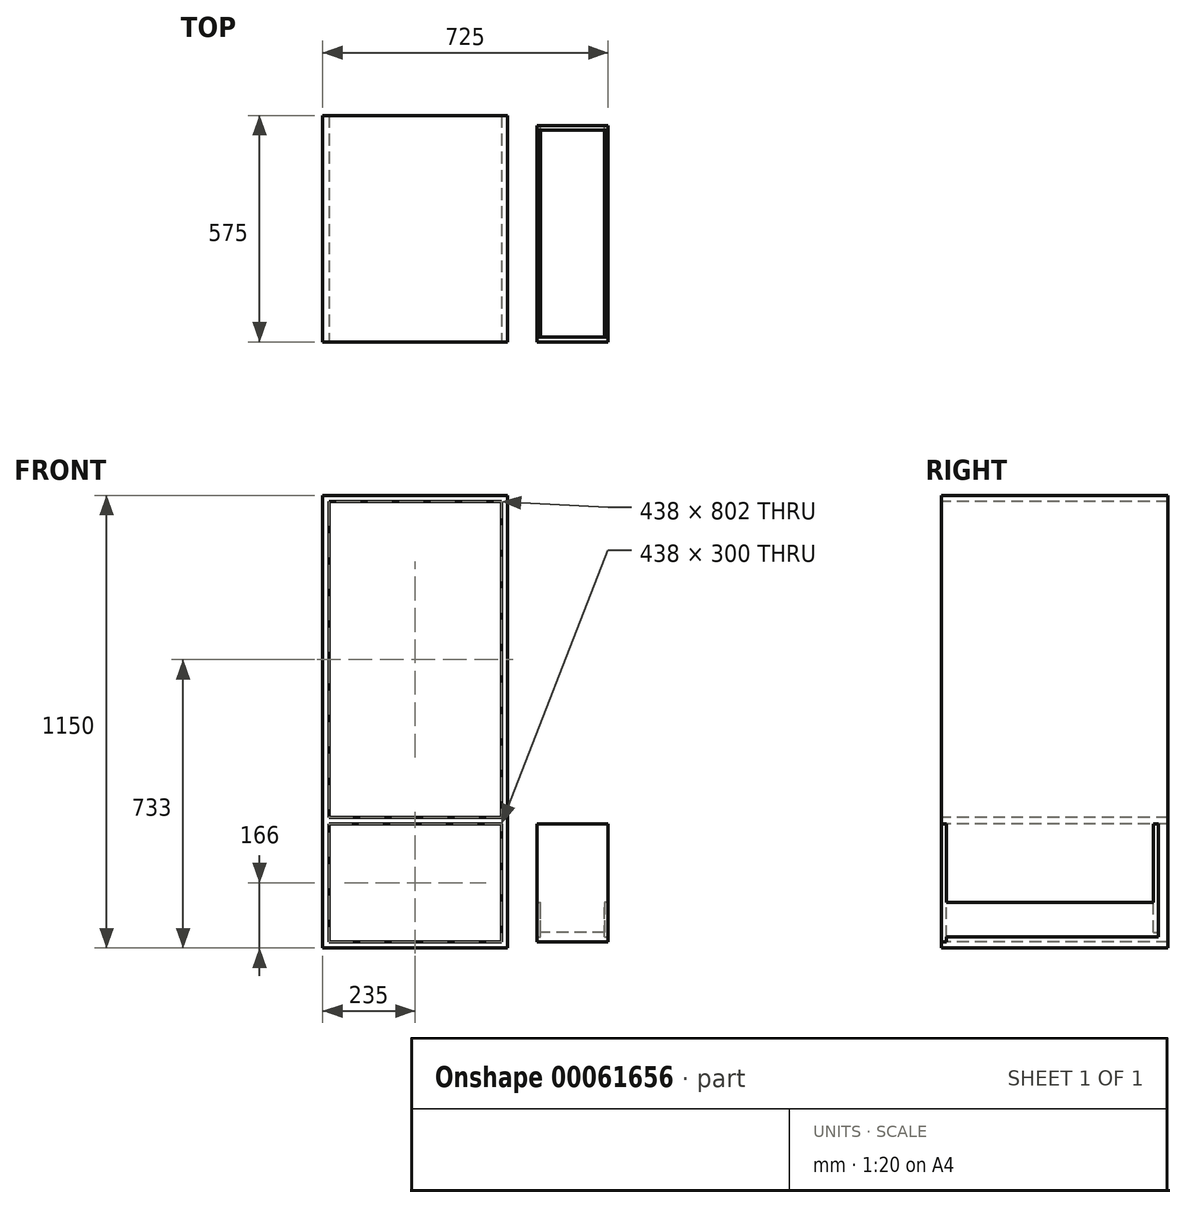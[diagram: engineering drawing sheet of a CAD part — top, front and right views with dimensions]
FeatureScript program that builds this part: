
annotation { "Feature Type Name" : "Feature", "Feature Type Description" : "" }
export const myFeature = defineFeature(function(context is Context, id is Id, definition is map)
    precondition{}
    {
        {
            var Q0;
            Q0=qCreatedBy(makeId("Front.planeOp"),FACE);
            var sketch = newSketch(context, id + "F0", { "sketchPlane" : qUnion([Q0])});
            skLineSegment(sketch, "E0.bottom", {"start": v(0, 0) * mm, "end": v(470, 0) * mm});
            skLineSegment(sketch, "E0.top", {"start": v(0, 1150) * mm, "end": v(470, 1150) * mm});
            skLineSegment(sketch, "E0.left", {"start": v(0, 0) * mm, "end": v(0, 1150) * mm});
            skLineSegment(sketch, "E0.right", {"start": v(470, 0) * mm, "end": v(470, 1150) * mm});
            skSolve(sketch);
        }
        {
            var Q0;
            Q0=makeQuery(id+"F0.imprint","IMPRINT",FACE,{"disambiguationData":[TD([[makeQuery(id+"F0.imprint","IMPRINT",EDGE,{"derivedFrom":sQuery(id+"F0.wireOp",EDGE,"E0.bottom")}),1.0]])]});
            extrude(context, id + "F1", {"entities" : qUnion([Q0]), "oppositeDirection" : true, "depth" : 575 * mm});
        }
        {
            var Q0;
            Q0=makeQuery(id+"F1.opExtrude","CAP_FACE",FACE,{"disambiguationData":[OSD([sQuery(id+"F0.wireOp",EDGE,"E0.bottom"),sQuery(id+"F0.wireOp",EDGE,"E0.top"),sQuery(id+"F0.wireOp",EDGE,"E0.left"),sQuery(id+"F0.wireOp",EDGE,"E0.right")])],"isStart":true});
            var sketch = newSketch(context, id + "F2", { "sketchPlane" : qUnion([Q0])});
            skLineSegment(sketch, "E1.0.0", {"start": v(0, 1150) * mm, "end": v(0, 0) * mm});
            skLineSegment(sketch, "E1.0.1", {"start": v(0, 0) * mm, "end": v(470, 0) * mm});
            skLineSegment(sketch, "E1.0.2", {"start": v(470, 0) * mm, "end": v(470, 1150) * mm});
            skLineSegment(sketch, "E1.0.3", {"start": v(470, 1150) * mm, "end": v(0, 1150) * mm});
            skLineSegment(sketch, "E2.0", {"start": v(16, 1134) * mm, "end": v(16, 16) * mm});
            skLineSegment(sketch, "E2.1", {"start": v(454, 1134) * mm, "end": v(16, 1134) * mm});
            skLineSegment(sketch, "E2.2", {"start": v(454, 16) * mm, "end": v(454, 1134) * mm});
            skLineSegment(sketch, "E2.3", {"start": v(16, 16) * mm, "end": v(454, 16) * mm});
            skSolve(sketch);
        }
        {
            var Q0;
            Q0=makeQuery(id+"F2.imprint","IMPRINT",FACE,{"disambiguationData":[TD([[makeQuery(id+"F2.imprint","IMPRINT",EDGE,{"derivedFrom":sQuery(id+"F2.wireOp",EDGE,"E2.0")}),1.0]])]});
            extrude(context, id + "F3", {"entities" : qUnion([Q0]), "operationType" : NewBodyOperationType.REMOVE, "oppositeDirection" : true, "depth" : 575 * mm});
        }
        {
            var Q0;
            Q0=makeQuery(id+"F1.opExtrude","CAP_FACE",FACE,{"disambiguationData":[OSD([sQuery(id+"F0.wireOp",EDGE,"E0.bottom"),sQuery(id+"F0.wireOp",EDGE,"E0.top"),sQuery(id+"F0.wireOp",EDGE,"E0.left"),sQuery(id+"F0.wireOp",EDGE,"E0.right")])],"isStart":true});
            var sketch = newSketch(context, id + "F4", { "sketchPlane" : qUnion([Q0])});
            skLineSegment(sketch, "E3.0", {"start": v(16, 1134) * mm, "end": v(16, 16) * mm});
            skLineSegment(sketch, "E3.1", {"start": v(454, 16) * mm, "end": v(454, 1134) * mm});
            skLineSegment(sketch, "E4.bottom", {"start": v(16, 316) * mm, "end": v(454, 316) * mm});
            skLineSegment(sketch, "E4.top", {"start": v(16, 332) * mm, "end": v(454, 332) * mm});
            skLineSegment(sketch, "E4.left", {"start": v(16, 316) * mm, "end": v(16, 332) * mm});
            skLineSegment(sketch, "E4.right", {"start": v(454, 316) * mm, "end": v(454, 332) * mm});
            skSolve(sketch);
        }
        {
            var Q0;
            Q0=makeQuery(id+"F4.imprint","IMPRINT",FACE,{"disambiguationData":[TD([[makeQuery(id+"F4.imprint","IMPRINT",EDGE,{"derivedFrom":sQuery(id+"F4.wireOp",EDGE,"E4.bottom")}),1.0]])]});
            extrude(context, id + "F5", {"entities" : qUnion([Q0]), "operationType" : NewBodyOperationType.ADD, "oppositeDirection" : true, "depth" : 575 * mm});
        }
        {
            var Q0;
            Q0=qCreatedBy(makeId("Front.planeOp"),FACE);
            var sketch = newSketch(context, id + "F6", { "sketchPlane" : qUnion([Q0])});
            skLineSegment(sketch, "E5.bottom", {"start": v(545, 16) * mm, "end": v(725, 16) * mm});
            skLineSegment(sketch, "E5.top", {"start": v(545, 316) * mm, "end": v(725, 316) * mm});
            skLineSegment(sketch, "E5.left", {"start": v(545, 16) * mm, "end": v(545, 316) * mm});
            skLineSegment(sketch, "E5.right", {"start": v(725, 16) * mm, "end": v(725, 316) * mm});
            skSolve(sketch);
        }
        {
            var Q0;
            Q0=makeQuery(id+"F6.imprint","IMPRINT",FACE,{"disambiguationData":[TD([[makeQuery(id+"F6.imprint","IMPRINT",EDGE,{"derivedFrom":sQuery(id+"F6.wireOp",EDGE,"E5.bottom")}),1.0]])]});
            extrude(context, id + "F7", {"entities" : qUnion([Q0]), "oppositeDirection" : true, "depth" : 12 * mm});
        }
        {
            var Q0;
            Q0=makeQuery(id+"F7.opExtrude","CAP_FACE",FACE,{"disambiguationData":[OSD([sQuery(id+"F6.wireOp",EDGE,"E5.bottom"),sQuery(id+"F6.wireOp",EDGE,"E5.top"),sQuery(id+"F6.wireOp",EDGE,"E5.left"),sQuery(id+"F6.wireOp",EDGE,"E5.right")])],"isStart":true});
            var sketch = newSketch(context, id + "F8", { "sketchPlane" : qUnion([Q0])});
            skLineSegment(sketch, "E6.0.0", {"start": v(545, 316) * mm, "end": v(545, 16) * mm});
            skLineSegment(sketch, "E6.0.1", {"start": v(545, 16) * mm, "end": v(725, 16) * mm});
            skLineSegment(sketch, "E6.0.2", {"start": v(725, 16) * mm, "end": v(725, 316) * mm});
            skLineSegment(sketch, "E6.0.3", {"start": v(725, 316) * mm, "end": v(545, 316) * mm});
            skLineSegment(sketch, "E7.bottom", {"start": v(545, 16) * mm, "end": v(554, 16) * mm});
            skLineSegment(sketch, "E7.top", {"start": v(545, 116) * mm, "end": v(554, 116) * mm});
            skLineSegment(sketch, "E7.left", {"start": v(545, 16) * mm, "end": v(545, 116) * mm});
            skLineSegment(sketch, "E7.right", {"start": v(554, 16) * mm, "end": v(554, 116) * mm});
            skLineSegment(sketch, "E8.bottom", {"start": v(725, 16) * mm, "end": v(716, 16) * mm});
            skLineSegment(sketch, "E8.top", {"start": v(725, 116) * mm, "end": v(716, 116) * mm});
            skLineSegment(sketch, "E8.left", {"start": v(725, 16) * mm, "end": v(725, 116) * mm});
            skLineSegment(sketch, "E8.right", {"start": v(716, 16) * mm, "end": v(716, 116) * mm});
            skLineSegment(sketch, "E9.top", {"start": v(545, 28) * mm, "end": v(725, 28) * mm});
            skLineSegment(sketch, "E9.left", {"start": v(545, 16) * mm, "end": v(545, 28) * mm});
            skLineSegment(sketch, "E9.right", {"start": v(725, 16) * mm, "end": v(725, 28) * mm});
            skLineSegment(sketch, "E10.bottom", {"start": v(554, 28) * mm, "end": v(716, 28) * mm});
            skLineSegment(sketch, "E10.top", {"start": v(554, 40) * mm, "end": v(716, 40) * mm});
            skLineSegment(sketch, "E10.left", {"start": v(554, 28) * mm, "end": v(554, 40) * mm});
            skLineSegment(sketch, "E10.right", {"start": v(716, 28) * mm, "end": v(716, 40) * mm});
            skSolve(sketch);
        }
        {
            var Q0;
            {var subQ4=sQuery(id+"F8.wireOp",EDGE,"E7.top");Q0=makeQuery(id+"F8.imprint","IMPRINT",FACE,{"disambiguationData":[TD([[makeQuery(id+"F8.imprint","IMPRINT",EDGE,{"derivedFrom":subQ4}),-1.0]])]});}
            var Q1;
            Q1=makeQuery(id+"F8.imprint","IMPRINT",FACE,{"disambiguationData":[TD([[makeQuery(id+"F8.imprint","IMPRINT",EDGE,{"derivedFrom":sQuery(id+"F8.wireOp",EDGE,"E10.bottom")}),1.0]])]});
            var Q2;
            {var subQ4=sQuery(id+"F8.wireOp",EDGE,"E8.top");Q2=makeQuery(id+"F8.imprint","IMPRINT",FACE,{"disambiguationData":[TD([[makeQuery(id+"F8.imprint","IMPRINT",EDGE,{"derivedFrom":subQ4}),1.0]])]});}
            extrude(context, id + "F9", {"entities" : qUnion([Q0, Q1, Q2]), "operationType" : NewBodyOperationType.ADD, "oppositeDirection" : true, "depth" : 550 * mm});
        }
        {
            var Q0;
            Q0=makeQuery(id+"F9.opExtrude","CAP_FACE",FACE,{"disambiguationData":[OSD([sQuery(id+"F8.wireOp",EDGE,"E7.top"),sQuery(id+"F8.wireOp",EDGE,"E7.left"),sQuery(id+"F8.wireOp",EDGE,"E7.right"),sQuery(id+"F8.wireOp",EDGE,"E8.top"),sQuery(id+"F8.wireOp",EDGE,"E8.left"),sQuery(id+"F8.wireOp",EDGE,"E8.right"),sQuery(id+"F8.wireOp",EDGE,"E9.top"),sQuery(id+"F8.wireOp",EDGE,"E10.bottom"),sQuery(id+"F8.wireOp",EDGE,"E10.top")])],"isStart":false});
            var sketch = newSketch(context, id + "F10", { "sketchPlane" : qUnion([Q0])});
            skLineSegment(sketch, "E11.0.0", {"start": v(-554, 116) * mm, "end": v(-545, 116) * mm});
            skLineSegment(sketch, "E11.0.1", {"start": v(-545, 116) * mm, "end": v(-545, 316) * mm});
            skLineSegment(sketch, "E11.0.2", {"start": v(-545, 316) * mm, "end": v(-725, 316) * mm});
            skLineSegment(sketch, "E11.0.3", {"start": v(-725, 316) * mm, "end": v(-725, 116) * mm});
            skLineSegment(sketch, "E11.0.4", {"start": v(-725, 116) * mm, "end": v(-716, 116) * mm});
            skLineSegment(sketch, "E11.0.5", {"start": v(-716, 116) * mm, "end": v(-716, 40) * mm});
            skLineSegment(sketch, "E11.0.6", {"start": v(-716, 40) * mm, "end": v(-554, 40) * mm});
            skLineSegment(sketch, "E11.0.7", {"start": v(-554, 40) * mm, "end": v(-554, 116) * mm});
            skLineSegment(sketch, "E12.0", {"start": v(-545, 16) * mm, "end": v(-725, 16) * mm});
            skLineSegment(sketch, "E13.bottom", {"start": v(-725, 16) * mm, "end": v(-545, 16) * mm});
            skLineSegment(sketch, "E13.top", {"start": v(-725, 316) * mm, "end": v(-545, 316) * mm});
            skLineSegment(sketch, "E13.left", {"start": v(-725, 16) * mm, "end": v(-725, 316) * mm});
            skLineSegment(sketch, "E13.right", {"start": v(-545, 16) * mm, "end": v(-545, 316) * mm});
            skSolve(sketch);
        }
        {
            var Q0;
            {var subQ1=sQuery(id+"F10.wireOp",EDGE,"E11.0.0");Q0=makeQuery(id+"F10.imprint","IMPRINT",FACE,{"disambiguationData":[TD([[makeQuery(id+"F10.imprint","IMPRINT",EDGE,{"derivedFrom":subQ1}),-1.0]])]});}
            var Q1;
            {var subQ0=sQuery(id+"F10.wireOp",EDGE,"E13.bottom");Q1=makeQuery(id+"F10.imprint","IMPRINT",FACE,{"disambiguationData":[TD([[makeQuery(id+"F10.imprint","IMPRINT",EDGE,{"derivedFrom":subQ0}),1.0]])]});}
            var Q2;
            {var subQ4=sQuery(id+"F10.wireOp",EDGE,"E11.0.0");Q2=makeQuery(id+"F10.imprint","IMPRINT",FACE,{"disambiguationData":[TD([[makeQuery(id+"F10.imprint","IMPRINT",EDGE,{"derivedFrom":subQ4}),1.0]])]});}
            extrude(context, id + "F11", {"entities" : qUnion([Q0, Q1, Q2]), "operationType" : NewBodyOperationType.ADD, "oppositeDirection" : true, "depth" : 12 * mm});
        }
    });
